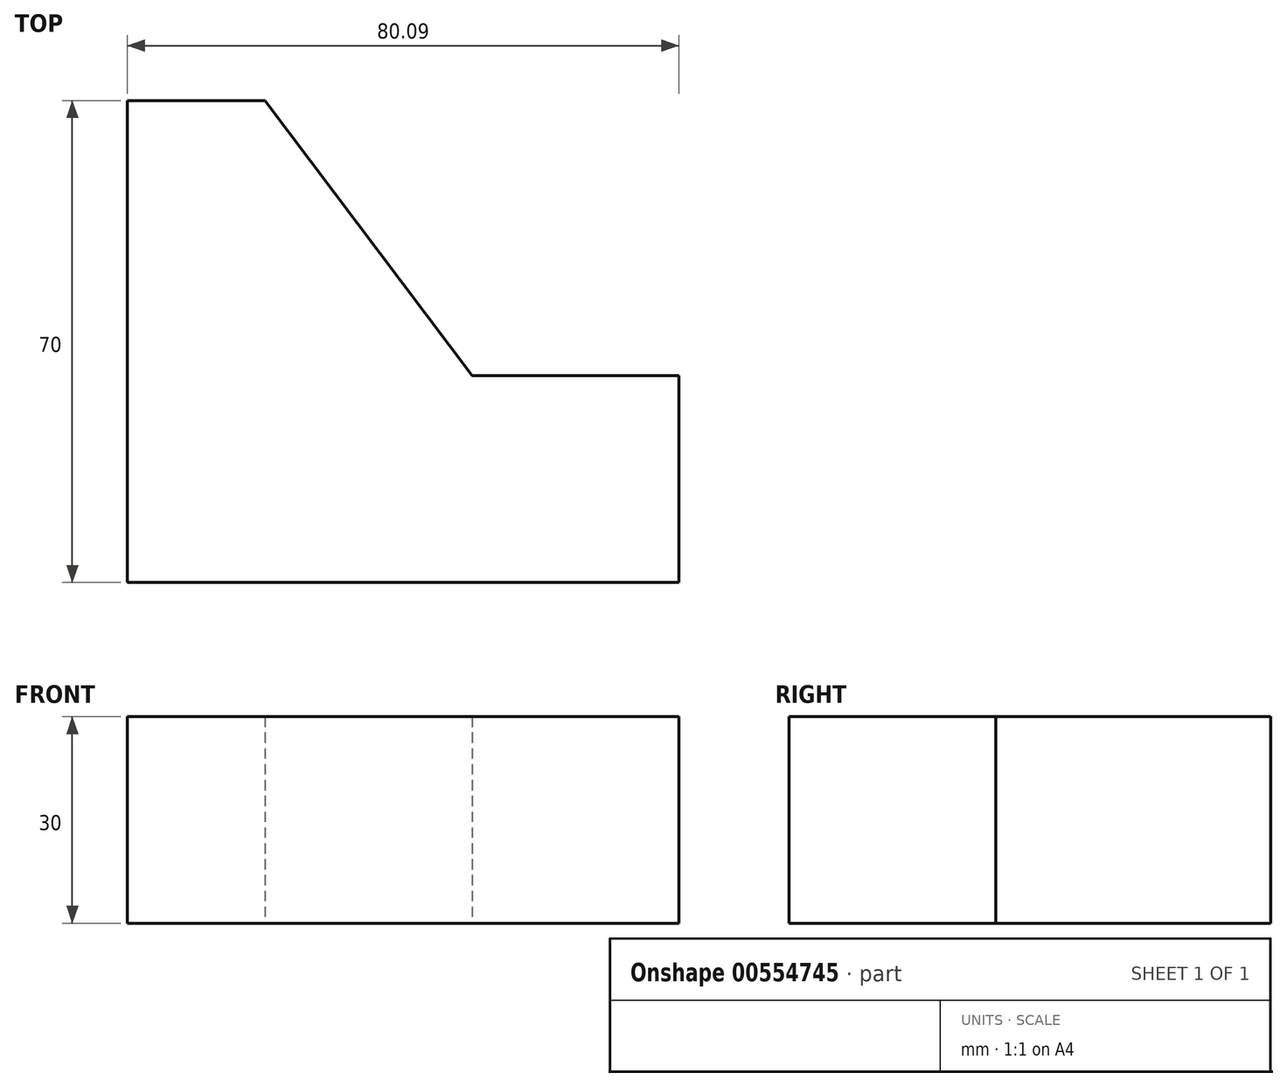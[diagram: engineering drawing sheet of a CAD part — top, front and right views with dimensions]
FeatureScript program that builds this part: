
annotation { "Feature Type Name" : "Feature", "Feature Type Description" : "" }
export const myFeature = defineFeature(function(context is Context, id is Id, definition is map)
    precondition{}
    {
        {
            var Q0;
            Q0=qCreatedBy(makeId("Top.planeOp"),FACE);
            var sketch = newSketch(context, id + "F0", { "sketchPlane" : qUnion([Q0])});
            skLineSegment(sketch, "E0", {"start": v(-50.44, 41.8) * mm, "end": v(-30.44, 41.8) * mm});
            skLineSegment(sketch, "E1", {"start": v(-30.44, 41.8) * mm, "end": v(-0.35, 1.86) * mm});
            skLineSegment(sketch, "E2", {"start": v(-0.35, 1.86) * mm, "end": v(29.65, 1.86) * mm});
            skLineSegment(sketch, "E3", {"start": v(-50.44, 41.8) * mm, "end": v(-50.44, -28.2) * mm});
            skLineSegment(sketch, "E4", {"start": v(-50.44, -28.2) * mm, "end": v(29.65, -28.2) * mm});
            skLineSegment(sketch, "E5", {"start": v(29.65, -28.2) * mm, "end": v(29.65, 1.86) * mm});
            skSolve(sketch);
        }
        {
            var Q0;
            Q0=makeQuery(id+"F0.imprint","IMPRINT",FACE,{"disambiguationData":[TD([[makeQuery(id+"F0.imprint","IMPRINT",EDGE,{"derivedFrom":sQuery(id+"F0.wireOp",EDGE,"E0")}),-1.0]])]});
            extrude(context, id + "F1", {"entities" : qUnion([Q0]), "depth" : 30 * mm, "offsetDistance" : 25 * mm});
        }
    });
